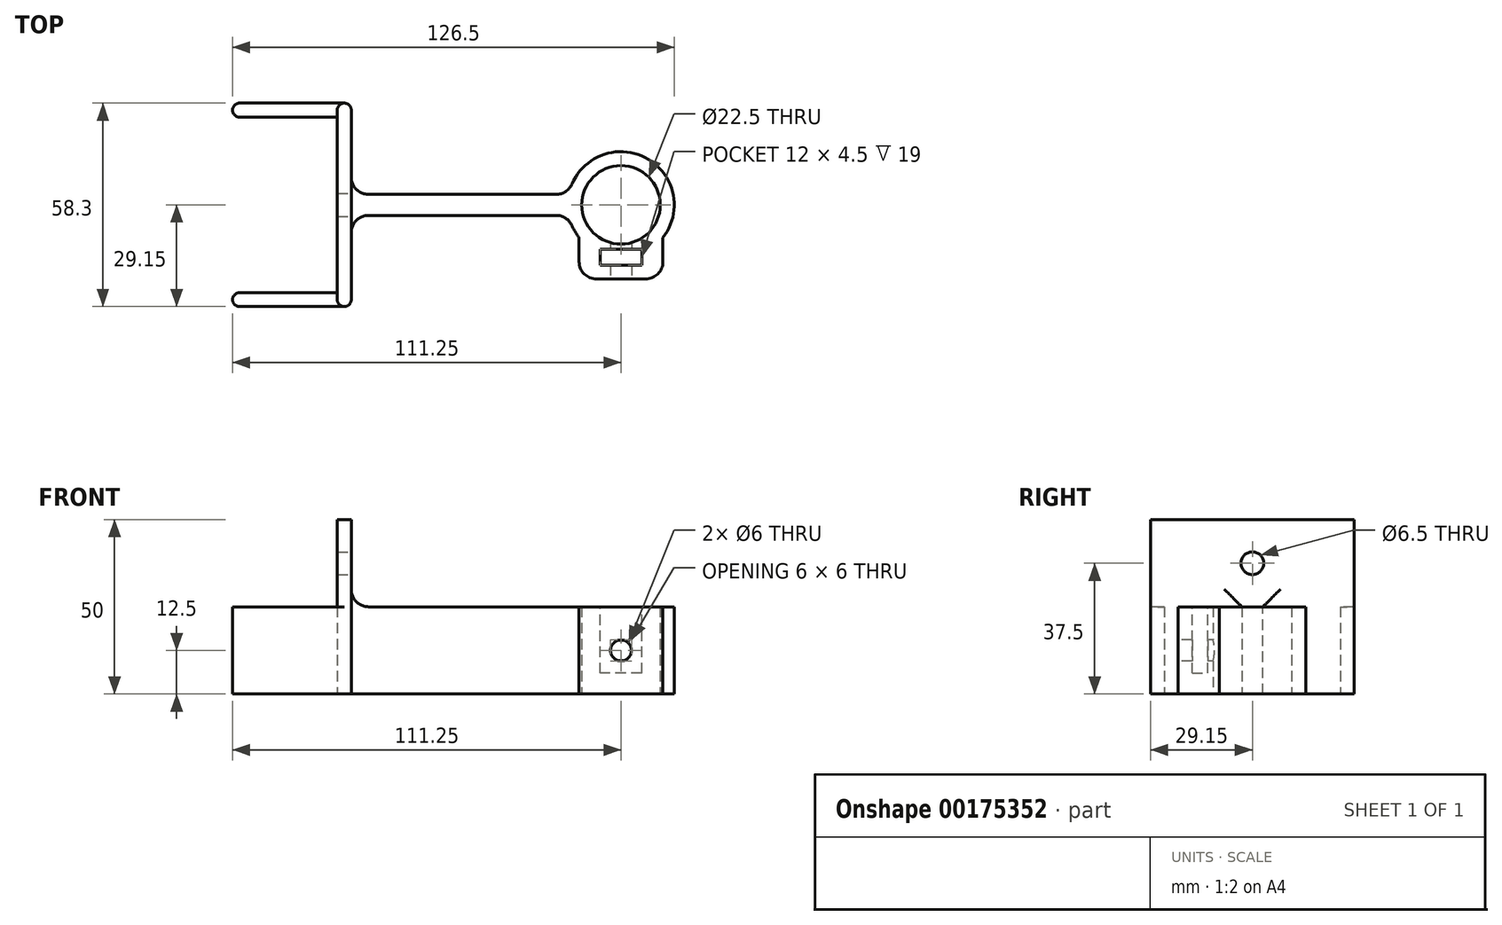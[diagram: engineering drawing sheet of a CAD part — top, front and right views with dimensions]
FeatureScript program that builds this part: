
annotation { "Feature Type Name" : "Feature", "Feature Type Description" : "" }
export const myFeature = defineFeature(function(context is Context, id is Id, definition is map)
    precondition{}
    {
        {
            var Q0;
            Q0=qCreatedBy(makeId("Top.planeOp"),FACE);
            var sketch = newSketch(context, id + "F0", { "sketchPlane" : qUnion([Q0])});
            skCircle(sketch, "E0", {"center": v(0, 0) * mm, "radius": 11.25 * mm});
            skLineSegment(sketch, "E1.bottom", {"start": v(-81.25, -25.15) * mm, "end": v(-111.25, -25.15) * mm});
            skLineSegment(sketch, "E1.top", {"start": v(-81.25, 25.15) * mm, "end": v(-111.25, 25.15) * mm});
            skLineSegment(sketch, "E1.left", {"start": v(-81.25, -25.15) * mm, "end": v(-81.25, 25.15) * mm});
            skPoint(sketch, "E1.middle", {"position": v(-96.25, 0) * mm});
            skLineSegment(sketch, "E2", {"start": v(-96.25, 0) * mm, "end": v(0, 0) * mm, "construction": true});
            skLineSegment(sketch, "E3.bottom", {"start": v(-14.95, -3) * mm, "end": v(-77.25, -3) * mm});
            skLineSegment(sketch, "E3.top", {"start": v(-14.95, 3) * mm, "end": v(-77.25, 3) * mm});
            skPoint(sketch, "E3.middle", {"position": v(-46.18, 0) * mm});
            skArc(sketch, "E4.0", {"start": v(-14.95, -3) * mm, "mid": v(-13.85, -6.38) * mm, "end": v(-12, -9.41) * mm});
            skLineSegment(sketch, "E5.0", {"start": v(-77.25, 29.15) * mm, "end": v(-111.25, 29.15) * mm});
            skLineSegment(sketch, "E5.1", {"start": v(-77.25, -29.15) * mm, "end": v(-77.25, -3) * mm});
            skLineSegment(sketch, "E5.2", {"start": v(-77.25, -29.15) * mm, "end": v(-111.25, -29.15) * mm});
            skLineSegment(sketch, "E6", {"start": v(-111.25, 25.15) * mm, "end": v(-111.25, 29.15) * mm});
            skLineSegment(sketch, "E7", {"start": v(-111.25, -29.15) * mm, "end": v(-111.25, -25.15) * mm});
            skPoint(sketch, "E8.orphan", {"position": v(-93.68, 3) * mm});
            skPoint(sketch, "E3.right.start.orphan", {"position": v(-93.68, -3) * mm});
            skLineSegment(sketch, "E9.trimOffspring", {"start": v(-77.25, 3) * mm, "end": v(-77.25, 29.15) * mm});
            skPoint(sketch, "E10.orphan", {"position": v(1.32, 3) * mm});
            skPoint(sketch, "E11.orphan", {"position": v(1.32, -3) * mm});
            skLineSegment(sketch, "E12.bottom", {"start": v(9, -21.25) * mm, "end": v(-9, -21.25) * mm});
            skPoint(sketch, "E12.middle", {"position": v(0, -11.25) * mm});
            skPoint(sketch, "E13.orphan", {"position": v(-9, -1.25) * mm});
            skPoint(sketch, "E14.orphan", {"position": v(9, -1.25) * mm});
            skArc(sketch, "E15.trimOffspring", {"start": v(12, -9.41) * mm, "mid": v(6.38, 13.85) * mm, "end": v(-14.95, 3) * mm});
            skLineSegment(sketch, "E16.0", {"start": v(-12, -21.25) * mm, "end": v(-12, -12.31) * mm});
            skLineSegment(sketch, "E16.2", {"start": v(12, -21.25) * mm, "end": v(12, -12.31) * mm});
            skLineSegment(sketch, "E17", {"start": v(-12, -12.31) * mm, "end": v(-12, -9.41) * mm});
            skLineSegment(sketch, "E18", {"start": v(12, -12.31) * mm, "end": v(12, -9.41) * mm});
            skLineSegment(sketch, "E19", {"start": v(9, -21.25) * mm, "end": v(12, -21.25) * mm});
            skLineSegment(sketch, "E20", {"start": v(-9, -21.25) * mm, "end": v(-12, -21.25) * mm});
            skSolve(sketch);
        }
        {
            var Q0;
            Q0=makeQuery(id+"F0.imprint","IMPRINT",FACE,{"disambiguationData":[TD([[makeQuery(id+"F0.imprint","IMPRINT",EDGE,{"derivedFrom":sQuery(id+"F0.wireOp",EDGE,"E0")}),-1.0]])]});
            extrude(context, id + "F1", {"entities" : qUnion([Q0]), "depth" : 25 * mm});
        }
        {
            var Q0;
            Q0=makeQuery(id+"F1.opExtrude","CAP_FACE",FACE,{"disambiguationData":[OSD([sQuery(id+"F0.wireOp",EDGE,"E0"),sQuery(id+"F0.wireOp",EDGE,"E1.bottom"),sQuery(id+"F0.wireOp",EDGE,"E1.top"),sQuery(id+"F0.wireOp",EDGE,"E1.left"),sQuery(id+"F0.wireOp",EDGE,"E3.bottom"),sQuery(id+"F0.wireOp",EDGE,"E3.top"),sQuery(id+"F0.wireOp",EDGE,"E4.0"),sQuery(id+"F0.wireOp",EDGE,"E5.0"),sQuery(id+"F0.wireOp",EDGE,"E5.1"),sQuery(id+"F0.wireOp",EDGE,"E5.2"),sQuery(id+"F0.wireOp",EDGE,"E6"),sQuery(id+"F0.wireOp",EDGE,"E7"),sQuery(id+"F0.wireOp",EDGE,"E9.trimOffspring"),sQuery(id+"F0.wireOp",EDGE,"E12.bottom"),sQuery(id+"F0.wireOp",EDGE,"E12.left"),sQuery(id+"F0.wireOp",EDGE,"E12.right"),sQuery(id+"F0.wireOp",EDGE,"E15.trimOffspring")])],"isStart":false});
            var sketch = newSketch(context, id + "F2", { "sketchPlane" : qUnion([Q0])});
            skLineSegment(sketch, "E21", {"start": v(-77.25, 29.15) * mm, "end": v(-77.25, -29.15) * mm});
            skLineSegment(sketch, "E22", {"start": v(-77.25, -29.15) * mm, "end": v(-81.25, -29.15) * mm});
            skLineSegment(sketch, "E23", {"start": v(-81.25, -29.15) * mm, "end": v(-81.25, 29.15) * mm});
            skLineSegment(sketch, "E24", {"start": v(-81.25, 29.15) * mm, "end": v(-77.25, 29.15) * mm});
            skSolve(sketch);
        }
        {
            var Q0;
            {var subQ0=sQuery(id+"F2.wireOp",EDGE,"E22");Q0=makeQuery(id+"F2.imprint","IMPRINT",FACE,{"disambiguationData":[TD([[makeQuery(id+"F2.imprint","IMPRINT",EDGE,{"derivedFrom":subQ0}),-1.0]])]});}
            extrude(context, id + "F3", {"entities" : qUnion([Q0]), "operationType" : NewBodyOperationType.ADD, "depth" : 25 * mm});
        }
        {
            var Q0;
            Q0=makeQuery(id+"F3.boolean.opBoolean","MERGE",FACE,{"derivedFrom":[makeQuery(id+"F1.opExtrude","SWEPT_FACE",FACE,{"disambiguationData":[OSD([sQuery(id+"F0.wireOp",EDGE,"E5.1")])]}),makeQuery(id+"F1.opExtrude","SWEPT_FACE",FACE,{"disambiguationData":[OSD([sQuery(id+"F0.wireOp",EDGE,"E9.trimOffspring")])]}),makeQuery(id+"F3.opExtrude","SWEPT_FACE",FACE,{"disambiguationData":[OSD([sQuery(id+"F2.wireOp",EDGE,"E21")])]})]});
            var sketch = newSketch(context, id + "F4", { "sketchPlane" : qUnion([Q0])});
            skLineSegment(sketch, "E25", {"start": v(0, 50) * mm, "end": v(0, 25) * mm, "construction": true});
            skCircle(sketch, "E26", {"center": v(0, 37.5) * mm, "radius": 3.25 * mm});
            skSolve(sketch);
        }
        {
            var Q0;
            Q0=makeQuery(id+"F4.imprint","IMPRINT",FACE,{"disambiguationData":[TD([[makeQuery(id+"F4.imprint","IMPRINT",EDGE,{"derivedFrom":sQuery(id+"F4.wireOp",EDGE,"E26")}),1.0]])]});
            extrude(context, id + "F5", {"entities" : qUnion([Q0]), "operationType" : NewBodyOperationType.REMOVE, "oppositeDirection" : true, "depth" : 4 * mm});
        }
        {
            var Q0;
            {var subQ0=sQuery(id+"F0.wireOp",EDGE,"E12.right");var subQ1=sQuery(id+"F0.wireOp",EDGE,"E5.1");var subQ2=sQuery(id+"F0.wireOp",EDGE,"E12.left");var subQ3=sQuery(id+"F0.wireOp",EDGE,"E12.bottom");var subQ4=sQuery(id+"F0.wireOp",EDGE,"E0");var subQ5=sQuery(id+"F0.wireOp",EDGE,"E15.trimOffspring");var subQ6=sQuery(id+"F0.wireOp",EDGE,"E3.bottom");var subQ7=sQuery(id+"F0.wireOp",EDGE,"E9.trimOffspring");var subQ8=sQuery(id+"F0.wireOp",EDGE,"E3.top");var subQ9=sQuery(id+"F0.wireOp",EDGE,"E4.0");Q0=makeQuery(id+"F3.boolean.opBoolean","SPLIT",FACE,{"disambiguationData":[TD([makeQuery(id+"F1.opExtrude","SWEPT_FACE",FACE,{"disambiguationData":[OSD([subQ4])]})])],"derivedFrom":makeQuery(id+"F1.opExtrude","CAP_FACE",FACE,{"disambiguationData":[OSD([subQ4,sQuery(id+"F0.wireOp",EDGE,"E1.bottom"),sQuery(id+"F0.wireOp",EDGE,"E1.top"),sQuery(id+"F0.wireOp",EDGE,"E1.left"),subQ6,subQ8,subQ9,sQuery(id+"F0.wireOp",EDGE,"E5.0"),subQ1,sQuery(id+"F0.wireOp",EDGE,"E5.2"),sQuery(id+"F0.wireOp",EDGE,"E6"),sQuery(id+"F0.wireOp",EDGE,"E7"),subQ7,subQ3,subQ2,subQ0,subQ5])],"isStart":false})});}
            var sketch = newSketch(context, id + "F6", { "sketchPlane" : qUnion([Q0])});
            skLineSegment(sketch, "E27.bottom", {"start": v(6, -17.25) * mm, "end": v(-6, -17.25) * mm});
            skLineSegment(sketch, "E27.top", {"start": v(6, -12.75) * mm, "end": v(-6, -12.75) * mm});
            skLineSegment(sketch, "E27.left", {"start": v(6, -17.25) * mm, "end": v(6, -12.75) * mm});
            skLineSegment(sketch, "E27.right", {"start": v(-6, -17.25) * mm, "end": v(-6, -12.75) * mm});
            skPoint(sketch, "E27.middle", {"position": v(0, -15) * mm});
            skSolve(sketch);
        }
        {
            var Q0;
            Q0=makeQuery(id+"F6.imprint","IMPRINT",FACE,{"disambiguationData":[TD([[makeQuery(id+"F6.imprint","IMPRINT",EDGE,{"derivedFrom":sQuery(id+"F6.wireOp",EDGE,"E27.bottom")}),-1.0]])]});
            extrude(context, id + "F7", {"entities" : qUnion([Q0]), "operationType" : NewBodyOperationType.REMOVE, "oppositeDirection" : true, "depth" : 19 * mm});
        }
        {
            var Q0;
            Q0=makeQuery(id+"F1.opExtrude","SWEPT_FACE",FACE,{"disambiguationData":[OSD([sQuery(id+"F0.wireOp",EDGE,"E12.bottom"),sQuery(id+"F0.wireOp",EDGE,"E19"),sQuery(id+"F0.wireOp",EDGE,"E20")])]});
            var sketch = newSketch(context, id + "F8", { "sketchPlane" : qUnion([Q0])});
            skLineSegment(sketch, "E28", {"start": v(0, 25) * mm, "end": v(0, 0) * mm, "construction": true});
            skCircle(sketch, "E29", {"center": v(0, 12.5) * mm, "radius": 3 * mm});
            skSolve(sketch);
        }
        {
            var Q0;
            Q0=makeQuery(id+"F8.imprint","IMPRINT",FACE,{"disambiguationData":[TD([[makeQuery(id+"F8.imprint","IMPRINT",EDGE,{"derivedFrom":sQuery(id+"F8.wireOp",EDGE,"E29")}),1.0]])]});
            var Q1;
            Q1=sQuery(id+"F8.wireOp",EDGE,"E29");
            extrude(context, id + "F9", {"entities" : qUnion([Q0]), "operationType" : NewBodyOperationType.REMOVE, "surfaceEntities" : qUnion([Q1]), "oppositeDirection" : true, "depth" : 12 * mm});
        }
        {
            var Q0;
            Q0=makeQuery(id+"F1.opExtrude","SWEPT_EDGE",EDGE,{"disambiguationData":[OSD([sQuery(id+"F0.wireOp",EDGE,"E16.2"),sQuery(id+"F0.wireOp",EDGE,"E19")])]});
            var Q1;
            Q1=makeQuery(id+"F1.opExtrude","SWEPT_EDGE",EDGE,{"disambiguationData":[OSD([sQuery(id+"F0.wireOp",EDGE,"E16.0"),sQuery(id+"F0.wireOp",EDGE,"E20")])]});
            var Q2;
            Q2=makeQuery(id+"F1.opExtrude","SWEPT_EDGE",EDGE,{"disambiguationData":[OSD([sQuery(id+"F0.wireOp",EDGE,"E3.bottom"),sQuery(id+"F0.wireOp",EDGE,"E5.1")])]});
            var Q3;
            Q3=makeQuery(id+"F1.opExtrude","SWEPT_EDGE",EDGE,{"disambiguationData":[OSD([sQuery(id+"F0.wireOp",EDGE,"E3.top"),sQuery(id+"F0.wireOp",EDGE,"E9.trimOffspring")])]});
            fillet(context, id + "F10", {"entities" : qUnion([Q0, Q1, Q2, Q3]), "radius" : 5 * mm, "tangentPropagation" : true, "allowEdgeOverflow" : false});
        }
        {
            var Q0;
            Q0=makeQuery(id+"F1.opExtrude","SWEPT_EDGE",EDGE,{"disambiguationData":[OSD([sQuery(id+"F0.wireOp",EDGE,"E3.top"),sQuery(id+"F0.wireOp",EDGE,"E15.trimOffspring")])]});
            var Q1;
            Q1=makeQuery(id+"F1.opExtrude","SWEPT_EDGE",EDGE,{"disambiguationData":[OSD([sQuery(id+"F0.wireOp",EDGE,"E3.bottom"),sQuery(id+"F0.wireOp",EDGE,"E4.0")])]});
            var Q2;
            Q2=makeQuery(id+"F3.opExtrude","CAP_EDGE",EDGE,{"disambiguationData":[OSD([sQuery(id+"F2.wireOp",EDGE,"E21")])],"isStart":true});
            fillet(context, id + "F11", {"entities" : qUnion([Q0, Q1, Q2]), "radius" : 5 * mm, "tangentPropagation" : true, "allowEdgeOverflow" : false});
        }
        {
            var Q0;
            Q0=makeQuery(id+"F1.opExtrude","SWEPT_EDGE",EDGE,{"disambiguationData":[OSD([sQuery(id+"F0.wireOp",EDGE,"E5.0"),sQuery(id+"F0.wireOp",EDGE,"E6")])]});
            var Q1;
            Q1=makeQuery(id+"F1.opExtrude","SWEPT_EDGE",EDGE,{"disambiguationData":[OSD([sQuery(id+"F0.wireOp",EDGE,"E1.bottom"),sQuery(id+"F0.wireOp",EDGE,"E7")])]});
            var Q2;
            Q2=makeQuery(id+"F1.opExtrude","SWEPT_EDGE",EDGE,{"disambiguationData":[OSD([sQuery(id+"F0.wireOp",EDGE,"E5.2"),sQuery(id+"F0.wireOp",EDGE,"E7")])]});
            var Q3;
            Q3=makeQuery(id+"F1.opExtrude","SWEPT_EDGE",EDGE,{"disambiguationData":[OSD([sQuery(id+"F0.wireOp",EDGE,"E1.top"),sQuery(id+"F0.wireOp",EDGE,"E6")])]});
            var Q4;
            Q4=makeQuery(id+"F3.boolean.opBoolean","MERGE",EDGE,{"derivedFrom":[makeQuery(id+"F1.opExtrude","SWEPT_EDGE",EDGE,{"disambiguationData":[OSD([sQuery(id+"F0.wireOp",EDGE,"E5.0"),sQuery(id+"F0.wireOp",EDGE,"E9.trimOffspring")])]}),makeQuery(id+"F3.opExtrude","SWEPT_EDGE",EDGE,{"disambiguationData":[OSD([sQuery(id+"F2.wireOp",EDGE,"E21"),sQuery(id+"F2.wireOp",EDGE,"E24")])]})]});
            var Q5;
            Q5=makeQuery(id+"F3.opExtrude","SWEPT_EDGE",EDGE,{"disambiguationData":[OSD([sQuery(id+"F0.wireOp",EDGE,"E5.0"),sQuery(id+"F2.wireOp",EDGE,"E23"),sQuery(id+"F2.wireOp",EDGE,"E24")])]});
            var Q6;
            Q6=makeQuery(id+"F3.boolean.opBoolean","MERGE",EDGE,{"derivedFrom":[makeQuery(id+"F1.opExtrude","SWEPT_EDGE",EDGE,{"disambiguationData":[OSD([sQuery(id+"F0.wireOp",EDGE,"E5.1"),sQuery(id+"F0.wireOp",EDGE,"E5.2")])]}),makeQuery(id+"F3.opExtrude","SWEPT_EDGE",EDGE,{"disambiguationData":[OSD([sQuery(id+"F2.wireOp",EDGE,"E21"),sQuery(id+"F2.wireOp",EDGE,"E22")])]})]});
            var Q7;
            Q7=makeQuery(id+"F3.opExtrude","SWEPT_EDGE",EDGE,{"disambiguationData":[OSD([sQuery(id+"F0.wireOp",EDGE,"E5.2"),sQuery(id+"F2.wireOp",EDGE,"E22"),sQuery(id+"F2.wireOp",EDGE,"E23")])]});
            fillet(context, id + "F12", {"entities" : qUnion([Q0, Q1, Q2, Q3, Q4, Q5, Q6, Q7]), "radius" : 2 * mm, "tangentPropagation" : true, "allowEdgeOverflow" : false});
        }
    });
